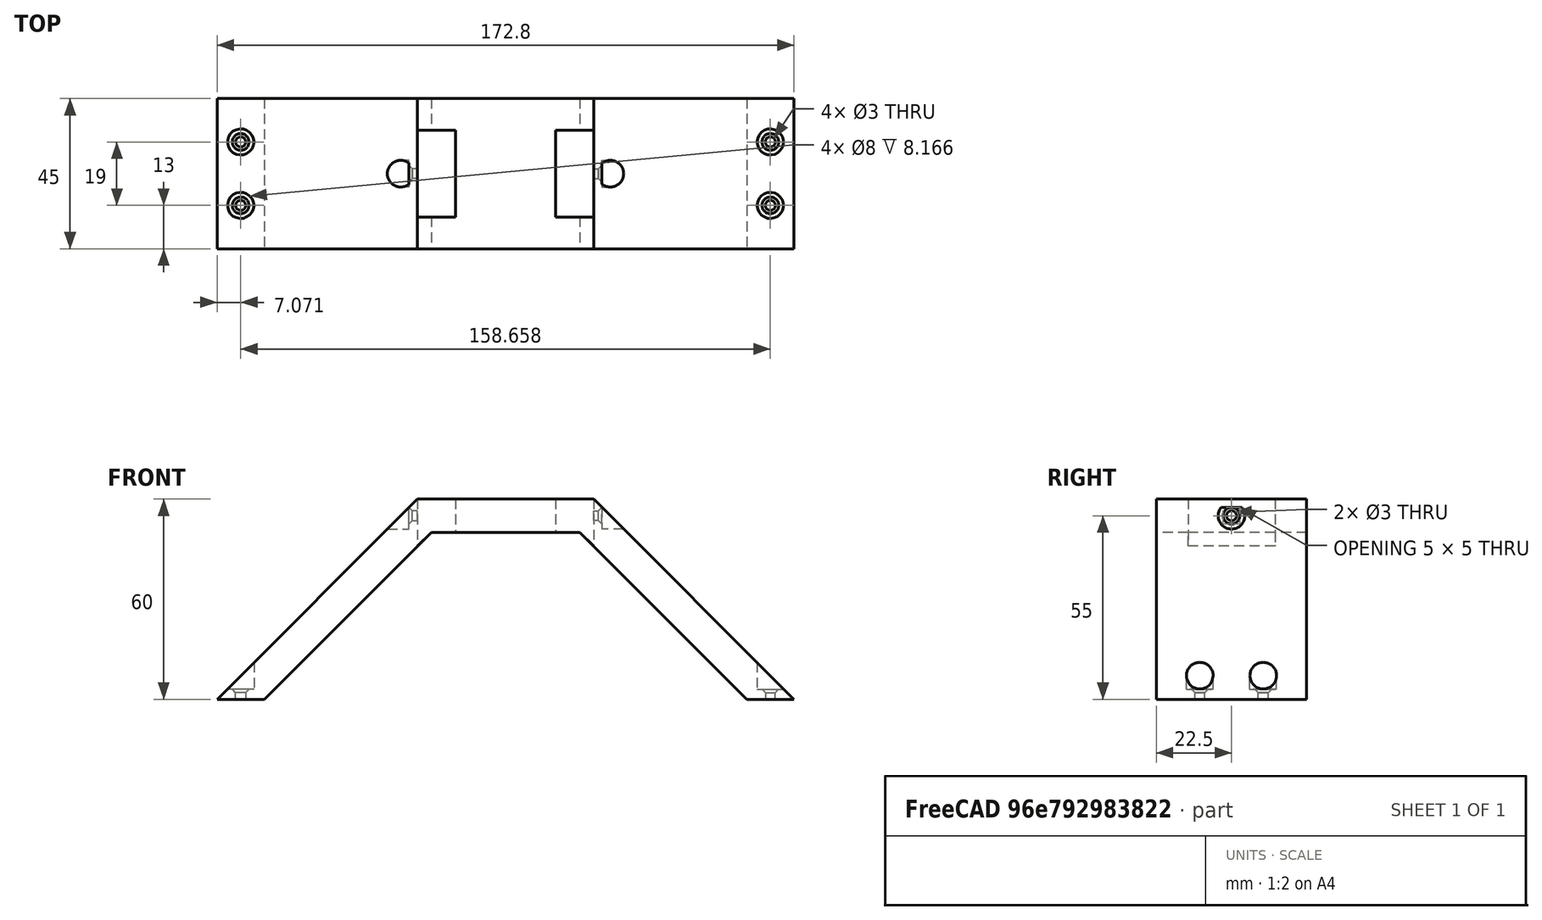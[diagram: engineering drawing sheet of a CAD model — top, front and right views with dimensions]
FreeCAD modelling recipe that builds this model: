
FCSTD DOCUMENT  (FreeCAD 0.19R24267 +99 (Git))
Label: Fuss
License: All rights reserved
LicenseURL: http://en.wikipedia.org/wiki/All_rights_reserved
objects: TechDraw::DrawViewDimension×16, Sketcher::SketchObject×6, PartDesign::Pocket×5, TechDraw::DrawProjGroupItem×4, TechDraw::DrawProjGroup×4, PartDesign::Plane×2, PartDesign::Chamfer×2, PartDesign::Mirrored×2, PartDesign::Pad×1, PartDesign::Body×1, TechDraw::DrawSVGTemplate×1, TechDraw::DrawViewDimExtent×1, TechDraw::DrawPage×1
note: 27 computed .brp shape members not serialized (recipe doc carries the construction recipe); baked Part::Feature solids carry a one-line shape summary decoded from their .brp

FEATURE [Sketcher::SketchObject] Sketch
  FullyConstrained = true
  MapMode = 5
  Placement = pos=(0,0,0) rot=(1,0,0;1.5708rad)
  Support = -> [XZ_Plane]
  sketch-geometry (15):
    g0: LineSegment StartX=-72.2579 StartY=0 StartZ=0 EndX=-86.4 EndY=0 EndZ=0
    g1: LineSegment StartX=-86.4 StartY=0 StartZ=0 EndX=-26.4 EndY=60 EndZ=0
    g2: LineSegment StartX=-26.4 StartY=60 StartZ=0 EndX=26.4 EndY=60 EndZ=0
    g3: LineSegment StartX=26.4 StartY=60 StartZ=0 EndX=86.4 EndY=0 EndZ=0
    g4: LineSegment StartX=86.4 StartY=0 StartZ=0 EndX=72.2579 EndY=0 EndZ=0
    g5: LineSegment StartX=72.2579 StartY=0 StartZ=0 EndX=22.2579 EndY=50 EndZ=0
    g6: LineSegment StartX=22.2579 StartY=50 StartZ=0 EndX=-22.2579 EndY=50 EndZ=0
    g7: LineSegment StartX=-22.2579 StartY=50 StartZ=0 EndX=-72.2579 EndY=0 EndZ=0
    g8: LineSegment StartX=-15 StartY=60 StartZ=0 EndX=-15 EndY=50 EndZ=0
    g9: LineSegment StartX=-26.4 StartY=60 StartZ=0 EndX=-26.4 EndY=45.8579 EndZ=0
    g10: LineSegment StartX=15 StartY=60 StartZ=0 EndX=15 EndY=50 EndZ=0
    g11: LineSegment StartX=26.4 StartY=60 StartZ=0 EndX=26.4 EndY=45.8579 EndZ=0
    g12: LineSegment StartX=-26.4 StartY=60 StartZ=0 EndX=-15 EndY=60 EndZ=0
    g13: LineSegment StartX=15 StartY=60 StartZ=0 EndX=26.4 EndY=60 EndZ=0
    g14: LineSegment StartX=72.2579 StartY=0 StartZ=0 EndX=79.3289 EndY=7.07107 EndZ=0
  constraints (43):
    c: PointOnObject(g0,g-1)
    c: PointOnObject(g0,g-1)
    c: Coincident(g0,g1)
    c: Coincident(g1,g2)
    c: Coincident(g2,g3)
    c: Coincident(g3,g4)
    c: Coincident(g4,g5)
    c: Coincident(g5,g6)
    c: Coincident(g6,g7)
    c: Coincident(g7,g0)
    c: Equal(g0,g4)
    c: Parallel(g1,g7)
    c: Horizontal(g2)
    c: Parallel(g5,g3)
    c: PointOnObject(g3,g-1)
    c: Symmetric(g6,g5,g-2)
    c: Angle(g-1,g7) = 0.785398
    c: Symmetric(g0,g4,g-2)
    c: PointOnObject(g8,g2)
    c: PointOnObject(g8,g6)
    c: Vertical(g8)
    c: Coincident(g9,g1)
    c: PointOnObject(g9,g7)
    c: Vertical(g9)
    c: DistanceX(g1,g8) = 11.4
    c: PointOnObject(g10,g2)
    c: PointOnObject(g10,g6)
    c: Vertical(g10)
    c: Coincident(g11,g2)
    c: PointOnObject(g11,g5)
    c: Vertical(g11)
    c: DistanceX(g8,g10) = 30
    c: Coincident(g12,g1)
    c: Coincident(g12,g8)
    c: Coincident(g13,g10)
    c: Coincident(g13,g2)
    c: Equal(g12,g13)
    c: Coincident(g14,g4)
    c: PointOnObject(g14,g3)
    c: Perpendicular(g3,g14)
    c: Equal(g10,g14)
    c: Distance(g14) = 10
    c: DistanceY(g-1,g6) = 50
FEATURE [PartDesign::Pad] Pad
  Direction = (1,1,1)
  Length = 45
  Length2 = 100
  Midplane = true
  Placement = pos=(0,0,0) rot=(1,0,0;1.5708rad)
  Profile = -> Sketch
  Type = 0
FEATURE [Sketcher::SketchObject] Sketch001
  ExternalGeometry = -> [Pad]
  FullyConstrained = true
  MapMode = 5
  Placement = pos=(0,3.97e-14,60) rot=(0,0,1;3.14159rad)
  Support = -> [Pad]
  sketch-geometry (8):
    g0: LineSegment StartX=-26.4 StartY=13 StartZ=0 EndX=-15 EndY=13 EndZ=0
    g1: LineSegment StartX=-15 StartY=13 StartZ=0 EndX=-15 EndY=-13 EndZ=0
    g2: LineSegment StartX=-15 StartY=-13 StartZ=0 EndX=-26.4 EndY=-13 EndZ=0
    g3: LineSegment StartX=-26.4 StartY=-13 StartZ=0 EndX=-26.4 EndY=13 EndZ=0
    g4: LineSegment StartX=15 StartY=13 StartZ=0 EndX=26.4 EndY=13 EndZ=0
    g5: LineSegment StartX=26.4 StartY=13 StartZ=0 EndX=26.4 EndY=-13 EndZ=0
    g6: LineSegment StartX=26.4 StartY=-13 StartZ=0 EndX=15 EndY=-13 EndZ=0
    g7: LineSegment StartX=15 StartY=-13 StartZ=0 EndX=15 EndY=13 EndZ=0
  constraints (23):
    c: Coincident(g0,g1)
    c: Coincident(g1,g2)
    c: Coincident(g2,g3)
    c: Coincident(g3,g0)
    c: Horizontal(g0)
    c: Horizontal(g2)
    c: Vertical(g1)
    c: Vertical(g3)
    c: Coincident(g4,g5)
    c: Coincident(g5,g6)
    c: Coincident(g6,g7)
    c: Coincident(g7,g4)
    c: Horizontal(g4)
    c: Horizontal(g6)
    c: Vertical(g5)
    c: PointOnObject(g5,g-3)
    c: DistanceY(g5,g5) = 26
    c: Symmetric(g4,g6,g-1)
    c: DistanceX(g4,g4) = 11.4
    c: PointOnObject(g2,g-4)
    c: Horizontal(g1,g6)
    c: Horizontal(g0,g4)
    c: Equal(g0,g4)
FEATURE [PartDesign::Pocket] Pocket
  BaseFeature = -> Pad
  Length = 50
  Length2 = 100
  Placement = pos=(0,0,0) rot=(1,0,0;1.5708rad)
  Profile = -> Sketch001
  Type = 0
FEATURE [PartDesign::Plane] DatumPlane
  AttachmentOffset = pos=(0,0,-20) rot=(0,0,1;0rad)
  Length = 98.0384
  MapMode = 5
  Placement = pos=(46.4,0,4.4e-15) rot=(0.707107,0,-0.707107;3.14159rad)
  ResizeMode = 0
  Support = -> [Pocket]
  Width = 63.0384
FEATURE [Sketcher::SketchObject] Sketch002
  ExternalGeometry = -> [Pocket]
  FullyConstrained = true
  MapMode = 5
  Placement = pos=(46.4,0,4.4e-15) rot=(0.707107,0,-0.707107;3.14159rad)
  Support = -> [DatumPlane]
  sketch-geometry (1):
    g0: Circle CenterX=-55 CenterY=0 CenterZ=0 NormalX=0 NormalY=0 NormalZ=1 AngleXU=0 Radius=1.5
  constraints (3):
    c: PointOnObject(g0,g-1)
    c: Diameter(g0) = 3
    c: DistanceX(g-3,g0) = 5
FEATURE [PartDesign::Pocket] Pocket001
  BaseFeature = -> Pocket
  Length = 20
  Length2 = 100
  Placement = pos=(0,0,0) rot=(1,0,0;1.5708rad)
  Profile = -> Sketch002
  Reversed = true
  Type = 0
FEATURE [Sketcher::SketchObject] Sketch003
  ExternalGeometry = -> [Pocket001]
  FullyConstrained = true
  MapMode = 5
  Placement = pos=(46.4,0,4.4e-15) rot=(0.707107,0,-0.707107;3.14159rad)
  Support = -> [DatumPlane]
  sketch-geometry (1):
    g0: Circle CenterX=-55 CenterY=-2.44e-14 CenterZ=0 NormalX=0 NormalY=0 NormalZ=1 AngleXU=0 Radius=4
  constraints (2):
    c: Coincident(g0,g-3)
    c: Diameter(g0) = 8
FEATURE [PartDesign::Pocket] Pocket002
  BaseFeature = -> Pocket001
  Length = 17.5
  Length2 = 100
  Placement = pos=(0,0,0) rot=(1,0,0;1.5708rad)
  Profile = -> Sketch003
  Reversed = true
  Type = 0
FEATURE [PartDesign::Chamfer] Chamfer
  Angle = 45
  Base = -> Pocket002 [Edge64]
  BaseFeature = -> Pocket002
  ChamferType = 0
  FlipDirection = false
  Placement = pos=(0,0,0) rot=(1,0,0;1.5708rad)
  Size = 1
  Size2 = 1
  SupportTransform = false
FEATURE [PartDesign::Mirrored] Mirrored
  BaseFeature = -> Chamfer
  MirrorPlane = -> YZ_Plane
  Originals = -> [Chamfer,Pocket002,Pocket001]
  Placement = pos=(0,0,0) rot=(1,0,0;1.5708rad)
FEATURE [PartDesign::Plane] DatumPlane001
  AttachmentOffset = pos=(0,0,-20) rot=(0,0,1;0rad)
  Length = 191.39
  MapMode = 5
  Placement = pos=(0,1.32e-14,20) rot=(1,0,0;3.14159rad)
  ResizeMode = 0
  Support = -> [Mirrored]
  Width = 68.5903
FEATURE [Sketcher::SketchObject] Sketch004
  ExternalGeometry = -> [Mirrored]
  FullyConstrained = true
  MapMode = 5
  Placement = pos=(0,1.32e-14,20) rot=(1,0,0;3.14159rad)
  Support = -> [DatumPlane001]
  sketch-geometry (3):
    g0: Circle CenterX=-79.3289 CenterY=-9.5 CenterZ=0 NormalX=0 NormalY=0 NormalZ=1 AngleXU=0 Radius=1.5
    g1: GeomPoint X=-79.3289 Y=22.5 Z=0
    g2: Circle CenterX=-79.3289 CenterY=9.5 CenterZ=0 NormalX=0 NormalY=0 NormalZ=1 AngleXU=0 Radius=1.5
  constraints (6):
    c: Symmetric(g-4,g-3,g1)
    c: Vertical(g0,g1)
    c: Diameter(g0) = 3
    c: Equal(g0,g2)
    c: Symmetric(g0,g2,g-1)
    c: DistanceY(g-5,g0) = 13
FEATURE [PartDesign::Pocket] Pocket003
  BaseFeature = -> Mirrored
  Length = 20
  Length2 = 100
  Placement = pos=(0,0,0) rot=(1,0,0;1.5708rad)
  Profile = -> Sketch004
  Reversed = true
  Type = 0
FEATURE [Sketcher::SketchObject] Sketch005
  ExternalGeometry = -> [Pocket003]
  FullyConstrained = true
  MapMode = 5
  Placement = pos=(0,1.32e-14,20) rot=(1,0,0;3.14159rad)
  Support = -> [DatumPlane001]
  sketch-geometry (2):
    g0: Circle CenterX=-79.3289 CenterY=9.5 CenterZ=0 NormalX=0 NormalY=0 NormalZ=1 AngleXU=0 Radius=4
    g1: Circle CenterX=-79.3289 CenterY=-9.5 CenterZ=0 NormalX=0 NormalY=0 NormalZ=1 AngleXU=0 Radius=4
  constraints (4):
    c: Coincident(g0,g-3)
    c: Coincident(g1,g-4)
    c: Equal(g1,g0)
    c: Diameter(g1) = 8
FEATURE [PartDesign::Pocket] Pocket004
  BaseFeature = -> Pocket003
  Length = 17
  Length2 = 100
  Placement = pos=(0,0,0) rot=(1,0,0;1.5708rad)
  Profile = -> Sketch005
  Reversed = true
  Type = 0
FEATURE [PartDesign::Chamfer] Chamfer001
  Angle = 45
  Base = -> Pocket004 [Edge90,Edge88]
  BaseFeature = -> Pocket004
  ChamferType = 0
  FlipDirection = false
  Placement = pos=(0,0,0) rot=(1,0,0;1.5708rad)
  Size = 1
  Size2 = 1
  SupportTransform = false
FEATURE [PartDesign::Mirrored] Mirrored001
  BaseFeature = -> Chamfer001
  MirrorPlane = -> Sketch004 [V_Axis]
  Originals = -> [Pocket003,Pocket004,Chamfer001]
  Placement = pos=(0,0,0) rot=(1,0,0;1.5708rad)
FEATURE [PartDesign::Body] Body
  Group = -> [Sketch,Pad,Sketch001,Pocket,DatumPlane,Sketch002,Pocket001,Sketch003,Pocket002,Chamfer,Mirrored,DatumPlane001,Sketch004,Pocket003,Sketch005,Pocket004,Chamfer001,Mirrored001]
  Origin = -> Origin
  Tip = -> Mirrored001
FEATURE [TechDraw::DrawSVGTemplate] Template
  Height = 210
  Orientation = 1
  Width = 297
FEATURE [TechDraw::DrawProjGroupItem] ProjItem  label="Seitenansicht (1:2)"
  Caption = Seitenansicht (1:2)
  CoarseView = false
  Direction = (0,-1,0)
  Focus = 100
  HardHidden = false
  IsoCount = 0
  IsoHidden = false
  IsoVisible = false
  LockPosition = true
  Perspective = false
  Rotation = 0
  RotationVector = (1,0,0)
  Scale = 0.5
  ScaleType = 2
  SeamHidden = false
  SeamVisible = true
  SmoothHidden = false
  SmoothVisible = true
  Source = -> [Body]
  Type = 0
  X = 0
  XDirection = (1,0,0)
  Y = 0
FEATURE [TechDraw::DrawProjGroup] ProjGroup
  Anchor = -> ProjItem
  AutoDistribute = true
  LockPosition = false
  ProjectionType = 0
  Rotation = 0
  Scale = 0.5
  ScaleType = 2
  Source = -> [Body]
  Views = -> [ProjItem]
  X = 74.5668
  Y = 162.773
  spacingX = 15
  spacingY = 15
FEATURE [TechDraw::DrawProjGroupItem] ProjItem001  label="Vorderansicht (1:1)"
  Caption = Vorderansicht (1:1)
  CoarseView = false
  Direction = (1,0,0)
  Focus = 100
  HardHidden = false
  IsoCount = 0
  IsoHidden = false
  IsoVisible = false
  LockPosition = true
  Perspective = false
  Rotation = 0
  RotationVector = (0,1,0)
  ScaleType = 2
  SeamHidden = false
  SeamVisible = true
  SmoothHidden = false
  SmoothVisible = true
  Source = -> [Body]
  Type = 0
  X = 0
  XDirection = (0,1,0)
  Y = 0
FEATURE [TechDraw::DrawProjGroup] ProjGroup001
  Anchor = -> ProjItem001
  AutoDistribute = true
  LockPosition = false
  ProjectionType = 0
  Rotation = 0
  ScaleType = 0
  Source = -> [Body]
  Views = -> [ProjItem001]
  X = 203.565
  Y = 155.619
  spacingX = 15
  spacingY = 15
FEATURE [TechDraw::DrawViewDimension] Dimension
  Arbitrary = false
  ArbitraryTolerances = false
  EqualTolerance = true
  FormatSpec = %.2f
  FormatSpecOverTolerance = %+.2f
  FormatSpecUnderTolerance = %+.2f
  Inverted = false
  LockPosition = false
  MeasureType = 1
  OverTolerance = 0
  References2D = -> [ProjItem]
  Rotation = 0
  ScaleType = 0
  TheoreticalExact = false
  Type = 1
  UnderTolerance = 0
  X = -22.6789
  Y = -8.43784
FEATURE [TechDraw::DrawViewDimension] Dimension001
  Arbitrary = false
  ArbitraryTolerances = false
  EqualTolerance = true
  FormatSpec = %.2f
  FormatSpecOverTolerance = %+.2f
  FormatSpecUnderTolerance = %+.2f
  Inverted = false
  LockPosition = false
  MeasureType = 1
  OverTolerance = 0
  References2D = -> [ProjItem]
  Rotation = 0
  ScaleType = 0
  TheoreticalExact = false
  Type = 1
  UnderTolerance = 0
  X = -1.18757
  Y = -8.76357
FEATURE [TechDraw::DrawViewDimension] Dimension002
  Arbitrary = false
  ArbitraryTolerances = false
  EqualTolerance = true
  FormatSpec = %.2f
  FormatSpecOverTolerance = %+.2f
  FormatSpecUnderTolerance = %+.2f
  Inverted = false
  LockPosition = false
  MeasureType = 1
  OverTolerance = 0
  References2D = -> [ProjItem]
  Rotation = 0
  ScaleType = 0
  TheoreticalExact = false
  Type = 1
  UnderTolerance = 0
  X = -24.4636
  Y = -15.7125
FEATURE [TechDraw::DrawViewDimension] Dimension003
  Arbitrary = false
  ArbitraryTolerances = false
  EqualTolerance = true
  FormatSpec = %.2f
  FormatSpecOverTolerance = %+.2f
  FormatSpecUnderTolerance = %+.2f
  Inverted = false
  LockPosition = false
  MeasureType = 1
  OverTolerance = 0
  References2D = -> [ProjItem]
  Rotation = 0
  ScaleType = 0
  TheoreticalExact = false
  Type = 1
  UnderTolerance = 0
  X = -0.250909
  Y = -27.7855
FEATURE [TechDraw::DrawViewDimension] Dimension004
  Arbitrary = false
  ArbitraryTolerances = false
  EqualTolerance = true
  FormatSpec = %.2f
  FormatSpecOverTolerance = %+.2f
  FormatSpecUnderTolerance = %+.2f
  Inverted = false
  LockPosition = false
  MeasureType = 1
  OverTolerance = 0
  References2D = -> [ProjItem]
  Rotation = 0
  ScaleType = 0
  TheoreticalExact = false
  Type = 2
  UnderTolerance = 0
  X = -49.8137
  Y = 1.6626
FEATURE [TechDraw::DrawViewDimension] Dimension005
  Arbitrary = false
  ArbitraryTolerances = false
  EqualTolerance = true
  FormatSpec = %.2f
  FormatSpecOverTolerance = %+.2f
  FormatSpecUnderTolerance = %+.2f
  Inverted = false
  LockPosition = false
  MeasureType = 1
  OverTolerance = 0
  References2D = -> [ProjItem]
  Rotation = 0
  ScaleType = 0
  TheoreticalExact = false
  Type = 1
  UnderTolerance = 0
  X = 0.950054
  Y = 27.8257
FEATURE [TechDraw::DrawViewDimension] Dimension006
  Arbitrary = false
  ArbitraryTolerances = false
  EqualTolerance = true
  FormatSpec = %.2f
  FormatSpecOverTolerance = %+.2f
  FormatSpecUnderTolerance = %+.2f
  Inverted = false
  LockPosition = false
  MeasureType = 1
  OverTolerance = 0
  References2D = -> [ProjItem]
  Rotation = 0
  ScaleType = 0
  TheoreticalExact = false
  Type = 2
  UnderTolerance = 0
  X = 36.8659
  Y = 3.23697
FEATURE [TechDraw::DrawViewDimension] Dimension007
  Arbitrary = false
  ArbitraryTolerances = false
  EqualTolerance = true
  FormatSpec = %.2f
  FormatSpecOverTolerance = %+.2f
  FormatSpecUnderTolerance = %+.2f
  Inverted = false
  LockPosition = false
  MeasureType = 1
  OverTolerance = 0
  References2D = -> [ProjItem001]
  Rotation = 0
  ScaleType = 0
  TheoreticalExact = false
  Type = 2
  UnderTolerance = 0
  X = 29.6254
  Y = -1.18757
FEATURE [TechDraw::DrawViewDimension] Dimension008
  Arbitrary = false
  ArbitraryTolerances = false
  EqualTolerance = true
  FormatSpec = %.2f
  FormatSpecOverTolerance = %+.2f
  FormatSpecUnderTolerance = %+.2f
  Inverted = false
  LockPosition = false
  MeasureType = 1
  OverTolerance = 0
  References2D = -> [ProjItem001]
  Rotation = 0
  ScaleType = 0
  TheoreticalExact = false
  Type = 1
  UnderTolerance = 0
  X = 1.24888
  Y = -38.6978
FEATURE [TechDraw::DrawViewDimension] Dimension009
  Arbitrary = false
  ArbitraryTolerances = false
  EqualTolerance = true
  FormatSpec = R%.2f
  FormatSpecOverTolerance = %+.2f
  FormatSpecUnderTolerance = %+.2f
  Inverted = false
  LockPosition = false
  MeasureType = 1
  OverTolerance = 0
  References2D = -> [ProjItem001]
  Rotation = 0
  ScaleType = 0
  TheoreticalExact = false
  Type = 4
  UnderTolerance = 0
  X = 15.2009
  Y = 22.0888
FEATURE [TechDraw::DrawViewDimension] Dimension010
  Arbitrary = false
  ArbitraryTolerances = false
  EqualTolerance = true
  FormatSpec = R%.2f
  FormatSpecOverTolerance = %+.2f
  FormatSpecUnderTolerance = %+.2f
  Inverted = false
  LockPosition = false
  MeasureType = 1
  OverTolerance = 0
  References2D = -> [ProjItem001]
  Rotation = 0
  ScaleType = 0
  TheoreticalExact = false
  Type = 4
  UnderTolerance = 0
  X = -27.0765
  Y = 18.051
FEATURE [TechDraw::DrawProjGroupItem] ProjItem002  label="Draufsicht (1:2)"
  Caption = Draufsicht (1:2)
  CoarseView = false
  Direction = (0,0,1)
  Focus = 100
  HardHidden = false
  IsoCount = 0
  IsoHidden = false
  IsoVisible = false
  LockPosition = true
  Perspective = false
  Rotation = 0
  RotationVector = (1,0,0)
  Scale = 0.5
  ScaleType = 2
  SeamHidden = false
  SeamVisible = true
  SmoothHidden = false
  SmoothVisible = true
  Source = -> [Body]
  Type = 0
  X = 0
  XDirection = (1,0,0)
  Y = 0
FEATURE [TechDraw::DrawProjGroup] ProjGroup002
  Anchor = -> ProjItem002
  AutoDistribute = true
  LockPosition = false
  ProjectionType = 0
  Rotation = 0
  Scale = 0.5
  ScaleType = 2
  Source = -> [Body]
  Views = -> [ProjItem002]
  X = 74.8162
  Y = 61.2892
  spacingX = 15
  spacingY = 15
FEATURE [TechDraw::DrawViewDimExtent] DimExtent
  Arbitrary = false
  ArbitraryTolerances = false
  CosmeticTags = 0be2aeb1-fc55-4a5b-b68a-e0a840358f46 | 62d3cd19-e069-433a-a60e-f8115b889cb7
  DirExtent = 0
  EqualTolerance = true
  FormatSpec = %.2f
  FormatSpecOverTolerance = %+.2f
  FormatSpecUnderTolerance = %+.2f
  Inverted = false
  LockPosition = false
  MeasureType = 1
  OverTolerance = 0
  References2D = -> [ProjItem002]
  Rotation = 0
  ScaleType = 0
  Source = -> [ProjItem002]
  TheoreticalExact = false
  Type = 1
  UnderTolerance = 0
  X = 1.24888
  Y = 42.7741
FEATURE [TechDraw::DrawViewDimension] Dimension011
  Arbitrary = false
  ArbitraryTolerances = false
  EqualTolerance = true
  FormatSpec = %.2f
  FormatSpecOverTolerance = %+.2f
  FormatSpecUnderTolerance = %+.2f
  Inverted = false
  LockPosition = false
  MeasureType = 1
  OverTolerance = 0
  References2D = -> [ProjItem002]
  Rotation = 0
  ScaleType = 0
  TheoreticalExact = false
  Type = 1
  UnderTolerance = 0
  X = -28.8244
  Y = 29.9832
FEATURE [TechDraw::DrawViewDimension] Dimension012
  Arbitrary = false
  ArbitraryTolerances = false
  EqualTolerance = true
  FormatSpec = %.2f
  FormatSpecOverTolerance = %+.2f
  FormatSpecUnderTolerance = %+.2f
  Inverted = false
  LockPosition = false
  MeasureType = 1
  OverTolerance = 0
  References2D = -> [ProjItem002]
  Rotation = 0
  ScaleType = 0
  TheoreticalExact = false
  Type = 1
  UnderTolerance = 0
  X = -0.62444
  Y = 29.9832
FEATURE [TechDraw::DrawViewDimension] Dimension013
  Arbitrary = false
  ArbitraryTolerances = false
  EqualTolerance = true
  FormatSpec = %.2f
  FormatSpecOverTolerance = %+.2f
  FormatSpecUnderTolerance = %+.2f
  Inverted = false
  LockPosition = false
  MeasureType = 1
  OverTolerance = 0
  References2D = -> [ProjItem]
  Rotation = 0
  ScaleType = 0
  TheoreticalExact = false
  Type = 1
  UnderTolerance = 0
  X = -32.5711
  Y = 27.4753
FEATURE [TechDraw::DrawViewDimension] Dimension014
  Arbitrary = false
  ArbitraryTolerances = false
  EqualTolerance = true
  FormatSpec = %.2f
  FormatSpecOverTolerance = %+.2f
  FormatSpecUnderTolerance = %+.2f
  Inverted = false
  LockPosition = false
  MeasureType = 1
  OverTolerance = 0
  References2D = -> [ProjItem002]
  Rotation = 0
  ScaleType = 0
  TheoreticalExact = false
  Type = 1
  UnderTolerance = 0
  X = -0.35897
  Y = 20.5499
FEATURE [TechDraw::DrawViewDimension] Dimension015
  Arbitrary = false
  ArbitraryTolerances = false
  EqualTolerance = true
  FormatSpec = %.2f
  FormatSpecOverTolerance = %+.2f
  FormatSpecUnderTolerance = %+.2f
  Inverted = false
  LockPosition = false
  MeasureType = 1
  OverTolerance = 0
  References2D = -> [ProjItem002]
  Rotation = 0
  ScaleType = 0
  TheoreticalExact = false
  Type = 2
  UnderTolerance = 0
  X = -1.88004
  Y = 1.24888
FEATURE [TechDraw::DrawProjGroupItem] ProjItem003  label="Schrägsicht"
  Caption = Schrägsicht
  CoarseView = false
  Direction = (0.5,-0.5,0.707)
  Focus = 100
  HardHidden = false
  IsoCount = 0
  IsoHidden = false
  IsoVisible = false
  LockPosition = true
  Perspective = false
  Rotation = 0
  RotationVector = (0.707,0.707,0)
  Scale = 0.333333
  ScaleType = 2
  SeamHidden = false
  SeamVisible = true
  SmoothHidden = false
  SmoothVisible = true
  Source = -> [Body]
  Type = 0
  X = 0
  XDirection = (0.707,0.707,0)
  Y = 0
FEATURE [TechDraw::DrawProjGroup] ProjGroup003
  Anchor = -> ProjItem003
  AutoDistribute = true
  LockPosition = false
  ProjectionType = 0
  Rotation = 0
  Scale = 0.333333
  ScaleType = 2
  Source = -> [Body]
  Views = -> [ProjItem003]
  X = 173.79
  Y = 79.7102
  spacingX = 15
  spacingY = 15
FEATURE [TechDraw::DrawPage] Page
  KeepUpdated = true
  NextBalloonIndex = 1
  ProjectionType = 0
  Template = -> Template
  Views = -> [ProjGroup,ProjGroup001,Dimension,Dimension001,Dimension002,Dimension003,Dimension004,Dimension005,Dimension006,Dimension007,Dimension008,Dimension009,Dimension010,ProjGroup002,DimExtent,Dimension011,Dimension012,Dimension013,Dimension014,Dimension015,ProjGroup003]
